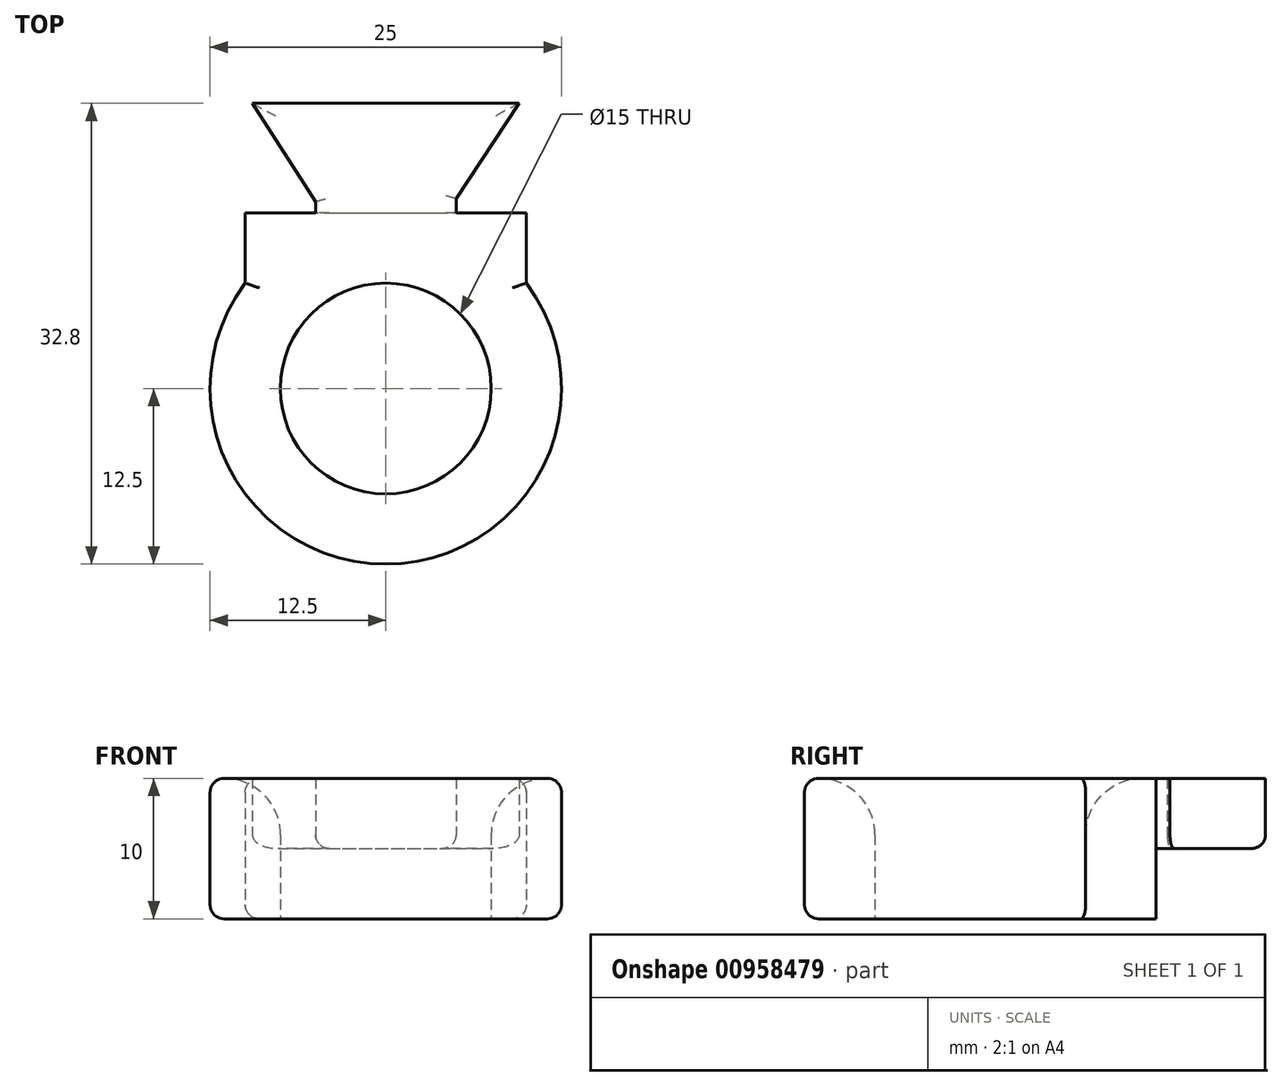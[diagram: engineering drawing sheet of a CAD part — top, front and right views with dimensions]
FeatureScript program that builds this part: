
annotation { "Feature Type Name" : "Feature", "Feature Type Description" : "" }
export const myFeature = defineFeature(function(context is Context, id is Id, definition is map)
    precondition{}
    {
        {
            var Q0;
            Q0=qCreatedBy(makeId("Top.planeOp"),FACE);
            var sketch = newSketch(context, id + "F0", { "sketchPlane" : qUnion([Q0])});
            skLineSegment(sketch, "E0.bottom", {"start": v(2.5, 25) * mm, "end": v(22.5, 25) * mm});
            skLineSegment(sketch, "E0.left", {"start": v(2.5, 25) * mm, "end": v(2.5, 20) * mm});
            skLineSegment(sketch, "E0.right", {"start": v(22.5, 25) * mm, "end": v(22.5, 20) * mm});
            skArc(sketch, "E1", {"start": v(2.5, 20) * mm, "mid": v(12.5, 0) * mm, "end": v(22.5, 20) * mm});
            skLineSegment(sketch, "E2.bottom", {"start": v(7.5, 25) * mm, "end": v(17.5, 25) * mm});
            skLineSegment(sketch, "E2.left", {"start": v(7.5, 25) * mm, "end": v(7.5, 25.8) * mm});
            skLineSegment(sketch, "E2.right", {"start": v(17.5, 25) * mm, "end": v(17.5, 26) * mm});
            skLineSegment(sketch, "E3", {"start": v(7.5, 25.8) * mm, "end": v(3, 32.8) * mm});
            skLineSegment(sketch, "E4", {"start": v(3, 32.8) * mm, "end": v(22, 32.8) * mm});
            skLineSegment(sketch, "E5", {"start": v(22, 32.8) * mm, "end": v(17.5, 26) * mm});
            skCircle(sketch, "E6", {"center": v(12.5, 12.5) * mm, "radius": 7.5 * mm});
            skSolve(sketch);
        }
        {
            var Q0;
            {var subQ1=sQuery(id+"F0.wireOp",EDGE,"E2.left");Q0=makeQuery(id+"F0.imprint","IMPRINT",FACE,{"disambiguationData":[TD([[makeQuery(id+"F0.imprint","IMPRINT",EDGE,{"derivedFrom":subQ1}),-1.0]])]});}
            extrude(context, id + "F1", {"entities" : qUnion([Q0]), "depth" : 10 * mm, "offsetDistance" : 25 * mm, "hasSecondDirection" : true, "secondDirectionOppositeDirection" : false, "secondDirectionDepth" : 5 * mm});
        }
        {
            var Q0;
            {var subQ0=sQuery(id+"F0.wireOp",EDGE,"E0.left");Q0=makeQuery(id+"F0.imprint","IMPRINT",FACE,{"disambiguationData":[TD([[makeQuery(id+"F0.imprint","IMPRINT",EDGE,{"derivedFrom":subQ0}),1.0]])]});}
            extrude(context, id + "F2", {"entities" : qUnion([Q0]), "operationType" : NewBodyOperationType.ADD, "depth" : 10 * mm, "offsetDistance" : 25 * mm});
        }
        {
            var Q0;
            Q0=makeQuery(id+"F1.opExtrude","CAP_EDGE",EDGE,{"disambiguationData":[OSD([sQuery(id+"F0.wireOp",EDGE,"E5")])],"isStart":true});
            var Q1;
            Q1=makeQuery(id+"F1.opExtrude","CAP_EDGE",EDGE,{"disambiguationData":[OSD([sQuery(id+"F0.wireOp",EDGE,"E2.right")])],"isStart":true});
            var Q2;
            Q2=makeQuery(id+"F1.opExtrude","CAP_EDGE",EDGE,{"disambiguationData":[OSD([sQuery(id+"F0.wireOp",EDGE,"E4")])],"isStart":true});
            var Q3;
            Q3=makeQuery(id+"F1.opExtrude","CAP_EDGE",EDGE,{"disambiguationData":[OSD([sQuery(id+"F0.wireOp",EDGE,"E3")])],"isStart":true});
            var Q4;
            Q4=makeQuery(id+"F1.opExtrude","CAP_EDGE",EDGE,{"disambiguationData":[OSD([sQuery(id+"F0.wireOp",EDGE,"E2.left")])],"isStart":true});
            var Q5;
            Q5=makeQuery(id+"F2.opExtrude","CAP_EDGE",EDGE,{"disambiguationData":[OSD([sQuery(id+"F0.wireOp",EDGE,"E1")])],"isStart":false});
            var Q6;
            Q6=makeQuery(id+"F2.opExtrude","CAP_EDGE",EDGE,{"disambiguationData":[OSD([sQuery(id+"F0.wireOp",EDGE,"E0.right")])],"isStart":false});
            var Q7;
            Q7=makeQuery(id+"F2.opExtrude","CAP_EDGE",EDGE,{"disambiguationData":[OSD([sQuery(id+"F0.wireOp",EDGE,"E0.left")])],"isStart":false});
            var Q8;
            Q8=makeQuery(id+"F2.opExtrude","CAP_EDGE",EDGE,{"disambiguationData":[OSD([sQuery(id+"F0.wireOp",EDGE,"E0.left")])],"isStart":true});
            var Q9;
            Q9=makeQuery(id+"F2.opExtrude","CAP_EDGE",EDGE,{"disambiguationData":[OSD([sQuery(id+"F0.wireOp",EDGE,"E1")])],"isStart":true});
            var Q10;
            Q10=makeQuery(id+"F2.opExtrude","CAP_EDGE",EDGE,{"disambiguationData":[OSD([sQuery(id+"F0.wireOp",EDGE,"E0.right")])],"isStart":true});
            fillet(context, id + "F3", {"entities" : qUnion([Q0, Q1, Q2, Q3, Q4, Q5, Q6, Q7, Q8, Q9, Q10]), "radius" : 1 * mm, "tangentPropagation" : true, "allowEdgeOverflow" : false});
        }
        {
            var Q0;
            Q0=makeQuery(id+"F2.opExtrude","CAP_EDGE",EDGE,{"disambiguationData":[OSD([sQuery(id+"F0.wireOp",EDGE,"E6")])],"isStart":false});
            fillet(context, id + "F4", {"entities" : qUnion([Q0]), "radius" : 4 * mm, "tangentPropagation" : true, "allowEdgeOverflow" : false});
        }
    });
